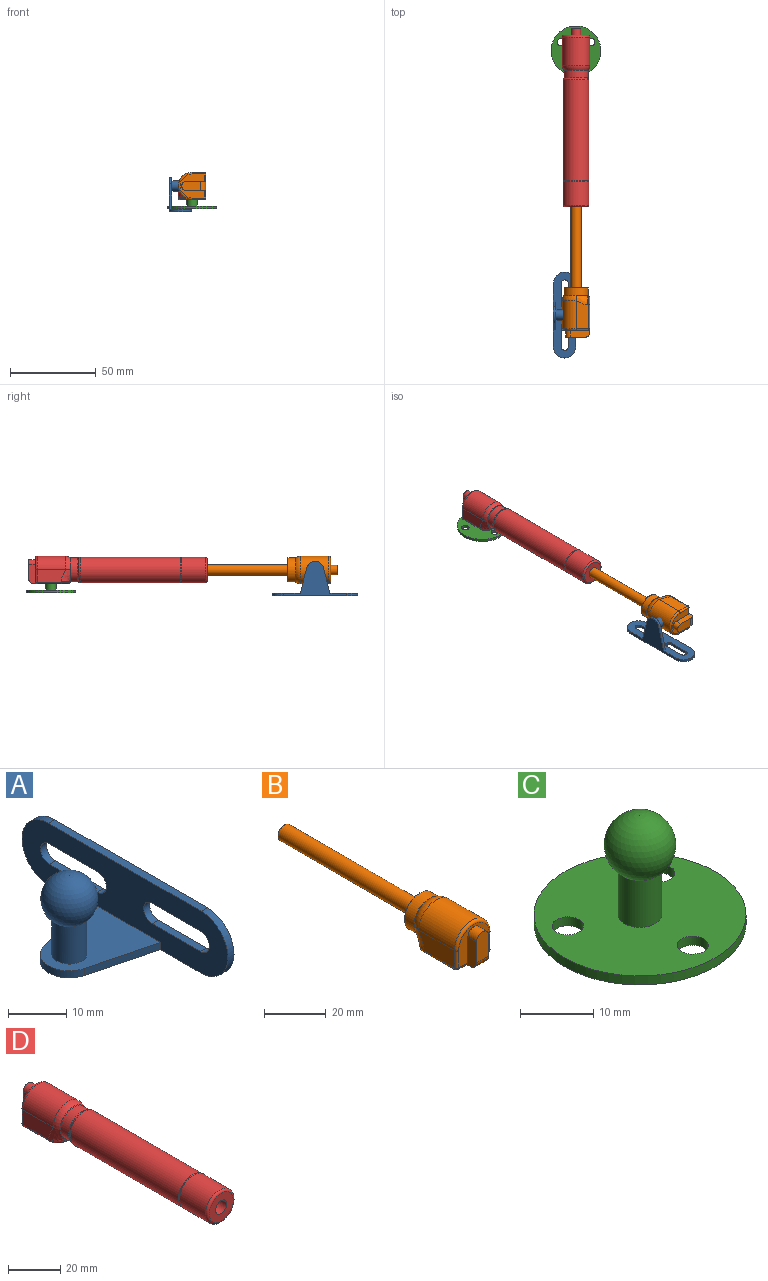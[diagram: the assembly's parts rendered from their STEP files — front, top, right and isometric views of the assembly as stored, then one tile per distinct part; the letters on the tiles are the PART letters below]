
ASSEMBLY  parts=4 mates=3
PART A: 20 faces, bbox 20x50x18.1 mm
  f0: sphere r=4.9mm, area 270.1mm2, adj f1
  f1: cylinder r=3mm len=7.8mm, axis (0,0,1), area 147mm2, adj f0,f4
  f2: plane 14.74x3.77mm, normal (-0.25,-0.97,0), area 22.8mm2, adj f4,f6,f7,f8
  f3: plane 14.74x3.77mm, normal (-0.25,0.97,0), area 22.8mm2, adj f4,f6,f7,f8
  f4: plane 18.5x17.23mm, normal (0,0,1), area 197.1mm2, adj f1,f2,f3,f6,f8
  f5: plane 50x13mm, normal (1,0,0), area 484.1mm2, adj f7,f9,f10,f11,f12,f13,f14,f15
  f6: cylinder r=5mm len=9.69mm, axis (0,0,1), area 19.8mm2, adj f2,f3,f4,f7
  f7: plane 37x20mm, normal (0,0,-1), area 280.9mm2, adj f2,f3,f5,f6,f8,f15,f16
  f8: plane 50x13mm, normal (-1,0,0), area 458.2mm2, adj f2,f3,f4,f7,f9,f10,f11,f12
  f9: cylinder r=2.15mm len=4.3mm, axis (1,0,0), area 10.1mm2, adj f5,f8,f10,f19
  f10: plane 11.7x1.5mm, normal (0,0,-1), area 17.5mm2, adj f5,f8,f9,f11
  f11: cylinder r=2.15mm len=4.3mm, axis (1,0,0), area 10.1mm2, adj f5,f8,f10,f19
  f12: cylinder r=2.15mm len=4.3mm, axis (1,0,0), area 10.1mm2, adj f5,f8,f13,f17
  f13: plane 11.7x1.5mm, normal (0,0,1), area 17.5mm2, adj f5,f8,f12,f14
  f14: cylinder r=2.15mm len=4.3mm, axis (1,0,0), area 10.1mm2, adj f5,f8,f13,f17
  f15: cylinder r=6.5mm len=13mm, axis (1,0,0), area 30.6mm2, adj f5,f7,f8,f18
  f16: cylinder r=6.5mm len=13mm, axis (1,0,0), area 30.6mm2, adj f5,f7,f8,f18
  f17: plane 11.7x1.5mm, normal (0,0,-1), area 17.5mm2, adj f5,f8,f12,f14
  f18: plane 37x1.5mm, normal (0,0,1), area 55.5mm2, adj f5,f8,f15,f16
  f19: plane 11.7x1.5mm, normal (0,0,1), area 17.5mm2, adj f5,f8,f9,f11
PART B: 39 faces, bbox 17.3x91x17.2 mm
  f0: plane 6x6mm, normal (0,1,0), area 28.3mm2, adj f1
  f1: cylinder r=3mm len=62mm, axis (0,-1,0), area 1168.7mm2, adj f0,f4
  f2: plane 0.31x0.13mm, normal (0,1,0), area 0mm2, adj f19,f20,f35
  f3: cylinder r=7mm len=14mm, axis (0,-1,0), area 189.1mm2, adj f13,f19
  f4: plane 13.6x13.6mm, normal (0,1,0), area 117mm2, adj f1,f13
  f5: plane 16.34x7mm, normal (1,0,0), area 104.9mm2, adj f6,f20,f21,f26,f31
  f6: cylinder r=8mm len=16.34mm, axis (0,-1,0), area 410.6mm2, adj f5,f7,f22,f27
  f7: plane 16.34x7mm, normal (-1,0,0), area 104.9mm2, adj f6,f23,f24,f29,f34
  f8: plane 20.09x14mm, normal (0,0,-1), area 177.8mm2, adj f11,f14,f15,f18,f25,f30,f31,f33
  f9: plane 0.31x0.13mm, normal (0,1,0), area 0mm2, adj f19,f23,f38
  f10: plane 14x14mm, normal (0,-1,0), area 106.7mm2, adj f14,f15,f16,f25,f26,f27,f29,f30
  f11: cylinder r=5mm len=10mm, axis (0,0,1), area 251.3mm2, adj f8,f12
  f12: sphere r=5mm, area 157.1mm2, adj f11
  f13: torus R=6.8mm, axis (0,-1,0), area 13.7mm2, adj f3,f4
  f14: plane 11.25x5mm, normal (-1,0,0), area 43.3mm2, adj f8,f10,f16,f17,f18,f30
  f15: plane 11.25x5mm, normal (1,0,0), area 43.3mm2, adj f8,f10,f16,f17,f18,f25
  f16: cylinder r=2.75mm len=5.5mm, axis (0,1,0), area 34.6mm2, adj f10,f14,f15,f17
  f17: plane 11x5.5mm, normal (0,-1,0), area 57.3mm2, adj f14,f15,f16,f18
  f18: cylinder r=3mm len=5.5mm, axis (1,0,0), area 25.9mm2, adj f8,f14,f15,f17
  f19: torus R=7.5mm, axis (0,-1,0), area 17.9mm2, adj f2,f3,f9,f21,f22,f24,f37
  f20: cylinder r=5mm len=5mm, axis (0,0,-1), area 1mm2, adj f2,f5,f21,f33
  f21: bspline ~9.63x5.39mm, area 34.5mm2, adj f5,f19,f20,f22
  f22: torus R=3mm, axis (0,1,0), area 74mm2, adj f6,f19,f21,f24
  f23: cylinder r=5mm len=5mm, axis (0,0,1), area 1mm2, adj f7,f9,f24,f36
  f24: bspline ~9.63x5.39mm, area 34.5mm2, adj f7,f19,f22,f23
  f25: cylinder r=1mm len=4.25mm, axis (-1,0,0), area 6.7mm2, adj f8,f10,f15,f28
  f26: cylinder r=1mm len=7mm, axis (0,0,-1), area 11mm2, adj f5,f10,f27,f28
  f27: torus R=7mm, axis (0,1,0), area 37.7mm2, adj f6,f10,f26,f29
  f28: sphere r=1mm, area 1.6mm2, adj f25,f26,f31
  f29: cylinder r=1mm len=7mm, axis (0,0,1), area 11mm2, adj f7,f10,f27,f32
  f30: cylinder r=1mm len=4.25mm, axis (-1,0,0), area 6.7mm2, adj f8,f10,f14,f32
  f31: cylinder r=1mm len=14mm, axis (0,-1,0), area 22mm2, adj f5,f8,f28,f33
  f32: sphere r=1mm, area 1.6mm2, adj f29,f30,f34
  f33: torus R=4mm, axis (0,0,-1), area 11.4mm2, adj f8,f20,f31,f35
  f34: cylinder r=1mm len=14mm, axis (0,-1,0), area 22mm2, adj f7,f8,f32,f36
  f35: cylinder r=1mm len=1mm, axis (-1,0,0), area 0.5mm2, adj f2,f8,f33,f37
  f36: torus R=4mm, axis (0,0,-1), area 11.4mm2, adj f8,f23,f34,f38
  f37: bspline ~6.07x1.14mm, area 7.3mm2, adj f8,f19,f35,f38
  f38: cylinder r=1mm len=1mm, axis (-1,0,0), area 0.5mm2, adj f8,f9,f36,f37
PART C: 8 faces, bbox 29x29x18.1 mm
  f0: sphere r=4.9mm, area 270.1mm2, adj f1
  f1: cylinder r=3mm len=7.8mm, axis (0,0,1), area 147mm2, adj f0,f7
  f2: cylinder r=2.12mm len=4.25mm, axis (0,0,1), area 20mm2, adj f6,f7
  f3: cylinder r=2.12mm len=4.25mm, axis (0,0,1), area 20mm2, adj f6,f7
  f4: cylinder r=2.12mm len=4.25mm, axis (0,0,1), area 20mm2, adj f6,f7
  f5: cylinder r=14.5mm len=29mm, axis (0,0,1), area 136.7mm2, adj f6,f7
  f6: plane 29x29mm, normal (0,0,-1), area 618mm2, adj f2,f3,f4,f5
  f7: plane 29x29mm, normal (0,0,1), area 589.7mm2, adj f1,f2,f3,f4,f5
PART D: 47 faces, bbox 17.3x104x17.2 mm
  f0: plane 13x13mm, normal (0,-1,0), area 104.5mm2, adj f7,f8
  f1: torus R=6.5mm, axis (0,1,0), area 70.4mm2, adj f2,f12
  f2: cylinder r=7.5mm len=58.5mm, axis (0,1,0), area 2756.7mm2, adj f1,f3
  f3: plane 15x15mm, normal (0,-1,0), area 4.7mm2, adj f2,f4
  f4: cylinder r=7.4mm len=14.8mm, axis (0,1,0), area 23.2mm2, adj f3,f5
  f5: plane 15x15mm, normal (0,1,0), area 4.7mm2, adj f4,f6
  f6: cylinder r=7.5mm len=15mm, axis (0,1,0), area 659.7mm2, adj f5,f7
  f7: torus R=6.5mm, axis (0,1,0), area 70.4mm2, adj f0,f6
  f8: cylinder r=3mm len=50mm, axis (0,-1,0), area 942.5mm2, adj f0,f9
  f9: plane 6x6mm, normal (0,-1,0), area 28.3mm2, adj f8
  f10: plane 0.31x0.13mm, normal (0,-1,0), area 0mm2, adj f27,f28,f43
  f11: cylinder r=7mm len=14mm, axis (0,1,0), area 189.1mm2, adj f21,f27
  f12: plane 13.6x13.6mm, normal (0,-1,0), area 12.5mm2, adj f1,f21
  f13: plane 16.34x7mm, normal (-1,0,0), area 104.9mm2, adj f14,f28,f29,f34,f39
  f14: cylinder r=8mm len=16.34mm, axis (0,1,0), area 410.6mm2, adj f13,f15,f30,f35
  f15: plane 16.34x7mm, normal (1,0,0), area 104.9mm2, adj f14,f31,f32,f37,f42
  f16: plane 20.09x14mm, normal (0,0,-1), area 177.8mm2, adj f19,f22,f23,f26,f33,f38,f39,f41
  f17: plane 0.31x0.13mm, normal (0,-1,0), area 0mm2, adj f27,f31,f46
  f18: plane 14x14mm, normal (0,1,0), area 106.7mm2, adj f22,f23,f24,f33,f34,f35,f37,f38
  f19: cylinder r=5mm len=10mm, axis (0,0,1), area 251.3mm2, adj f16,f20
  f20: sphere r=5mm, area 157.1mm2, adj f19
  f21: torus R=6.8mm, axis (0,1,0), area 13.7mm2, adj f11,f12
  f22: plane 11.25x5mm, normal (1,0,0), area 43.3mm2, adj f16,f18,f24,f25,f26,f38
  f23: plane 11.25x5mm, normal (-1,0,0), area 43.3mm2, adj f16,f18,f24,f25,f26,f33
  f24: cylinder r=2.75mm len=5.5mm, axis (0,-1,0), area 34.6mm2, adj f18,f22,f23,f25
  f25: plane 11x5.5mm, normal (0,1,0), area 57.3mm2, adj f22,f23,f24,f26
  f26: cylinder r=3mm len=5.5mm, axis (-1,0,0), area 25.9mm2, adj f16,f22,f23,f25
  f27: torus R=7.5mm, axis (0,1,0), area 17.9mm2, adj f10,f11,f17,f29,f30,f32,f45
  f28: cylinder r=5mm len=5mm, axis (0,0,-1), area 1mm2, adj f10,f13,f29,f41
  f29: bspline ~9.63x5.39mm, area 34.5mm2, adj f13,f27,f28,f30
  f30: torus R=3mm, axis (0,-1,0), area 74mm2, adj f14,f27,f29,f32
  f31: cylinder r=5mm len=5mm, axis (0,0,1), area 1mm2, adj f15,f17,f32,f44
  f32: bspline ~8.53x5.39mm, area 34.5mm2, adj f15,f27,f30,f31
  f33: cylinder r=1mm len=4.25mm, axis (1,0,0), area 6.7mm2, adj f16,f18,f23,f36
  f34: cylinder r=1mm len=7mm, axis (0,0,-1), area 11mm2, adj f13,f18,f35,f36
  f35: torus R=7mm, axis (0,-1,0), area 37.7mm2, adj f14,f18,f34,f37
  f36: sphere r=1mm, area 1.6mm2, adj f33,f34,f39
  f37: cylinder r=1mm len=7mm, axis (0,0,1), area 11mm2, adj f15,f18,f35,f40
  f38: cylinder r=1mm len=4.25mm, axis (1,0,0), area 6.7mm2, adj f16,f18,f22,f40
  f39: cylinder r=1mm len=14mm, axis (0,1,0), area 22mm2, adj f13,f16,f36,f41
  f40: sphere r=1mm, area 1.6mm2, adj f37,f38,f42
  f41: torus R=4mm, axis (0,0,-1), area 11.4mm2, adj f16,f28,f39,f43
  f42: cylinder r=1mm len=14mm, axis (0,1,0), area 22mm2, adj f15,f16,f40,f44
  f43: cylinder r=1mm len=1mm, axis (1,0,0), area 0.5mm2, adj f10,f16,f41,f45
  f44: torus R=4mm, axis (0,0,-1), area 11.4mm2, adj f16,f31,f42,f46
  f45: bspline ~6.07x1.14mm, area 7.3mm2, adj f16,f27,f43,f46
  f46: cylinder r=1mm len=1mm, axis (1,0,0), area 0.5mm2, adj f16,f17,f44,f45
PLACE A rot(axis=(0,1,0),90deg) t=(0,-63,0)mm
PLACE B rot(axis=(0,-1,0),90deg) t=(0,0,0)mm
PLACE C t=(0,91,0)mm
PLACE D at identity fixed
MATE ball A.f6 <-> B.f11  axis (1,0,0) through (0,-63,0)mm
MATE slider B.f1 <-> D.f8  axis (0,-1,0) through (0,0,0)mm
MATE ball C.f1 <-> D.f19  axis (0,0,1) through (0,91,0)mm
